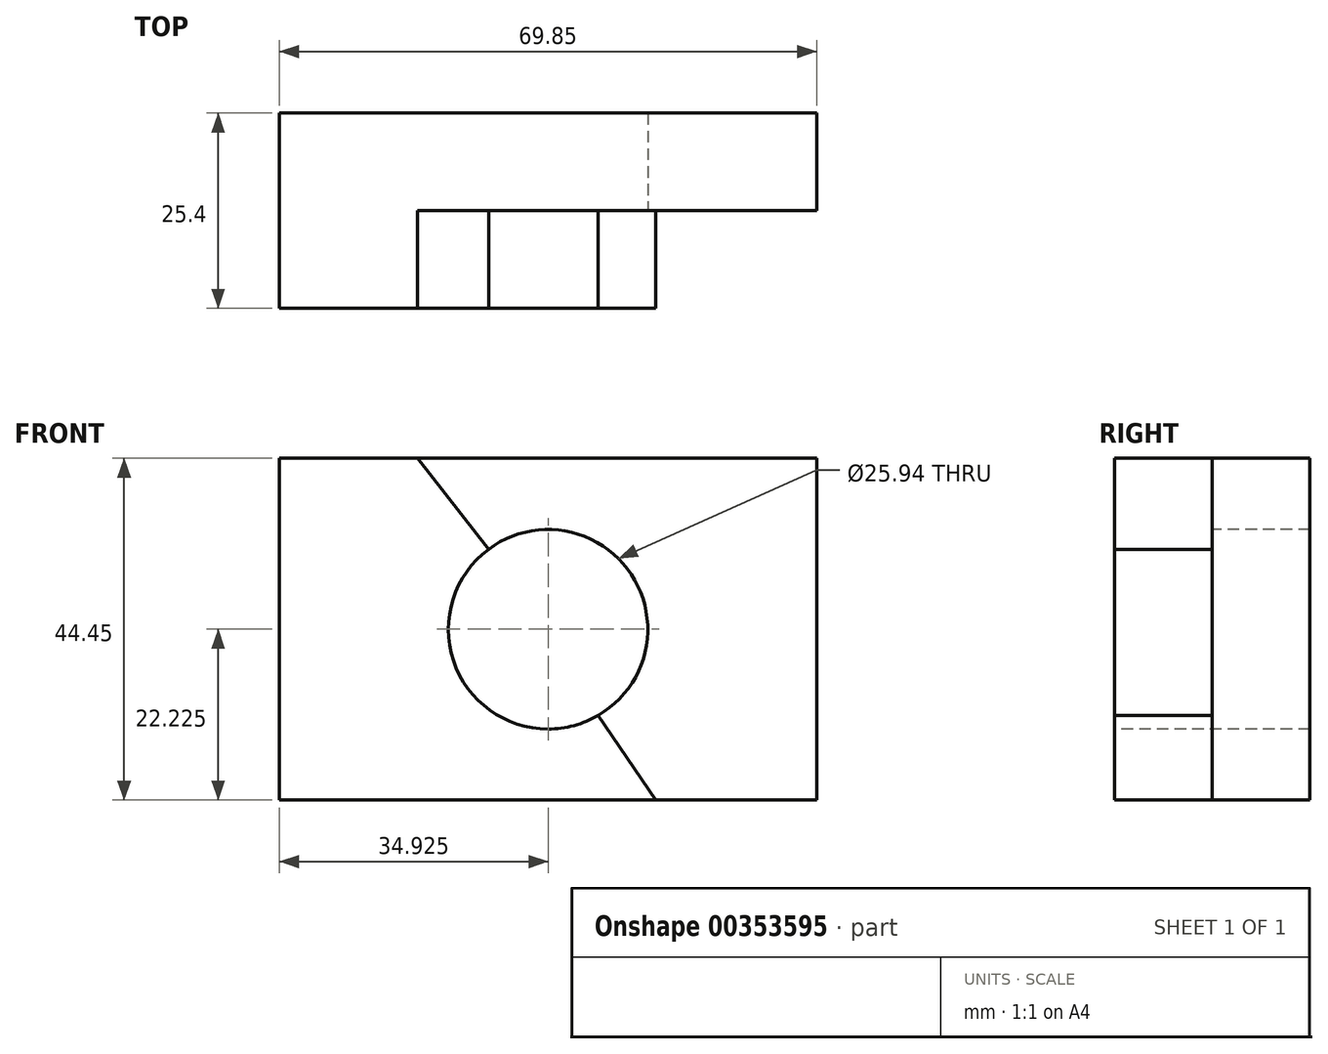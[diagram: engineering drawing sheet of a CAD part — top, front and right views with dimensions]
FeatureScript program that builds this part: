
annotation { "Feature Type Name" : "Feature", "Feature Type Description" : "" }
export const myFeature = defineFeature(function(context is Context, id is Id, definition is map)
    precondition{}
    {
        {
            var Q0;
            Q0=qCreatedBy(makeId("Front.planeOp"),FACE);
            var sketch = newSketch(context, id + "F0", { "sketchPlane" : qUnion([Q0])});
            skLineSegment(sketch, "E0.bottom", {"start": v(0, 0) * mm, "end": v(69.85, 0) * mm});
            skLineSegment(sketch, "E0.top", {"start": v(0, 44.45) * mm, "end": v(69.85, 44.45) * mm});
            skLineSegment(sketch, "E0.left", {"start": v(0, 0) * mm, "end": v(0, 44.45) * mm});
            skLineSegment(sketch, "E0.right", {"start": v(69.85, 0) * mm, "end": v(69.85, 44.45) * mm});
            skSolve(sketch);
        }
        {
            var Q0;
            Q0=makeQuery(id+"F0.imprint","IMPRINT",FACE,{"disambiguationData":[TD([[makeQuery(id+"F0.imprint","IMPRINT",EDGE,{"derivedFrom":sQuery(id+"F0.wireOp",EDGE,"E0.bottom")}),1.0]])]});
            extrude(context, id + "F1", {"entities" : qUnion([Q0]), "depth" : 12.7 * mm});
        }
        {
            var Q0;
            Q0=makeQuery(id+"F1.opExtrude","CAP_FACE",FACE,{"disambiguationData":[OSD([sQuery(id+"F0.wireOp",EDGE,"E0.bottom"),sQuery(id+"F0.wireOp",EDGE,"E0.top"),sQuery(id+"F0.wireOp",EDGE,"E0.left"),sQuery(id+"F0.wireOp",EDGE,"E0.right")])],"isStart":false});
            var sketch = newSketch(context, id + "F2", { "sketchPlane" : qUnion([Q0])});
            skCircle(sketch, "E1", {"center": v(34.92, 22.23) * mm, "radius": 12.97 * mm});
            skPoint(sketch, "E1.centerSnap0", {"position": v(69.85, 22.23) * mm});
            skPoint(sketch, "E1.centerSnap1", {"position": v(34.92, 44.45) * mm});
            skSolve(sketch);
        }
        {
            var Q0;
            Q0=makeQuery(id+"F2.imprint","IMPRINT",FACE,{"disambiguationData":[TD([[makeQuery(id+"F2.imprint","IMPRINT",EDGE,{"derivedFrom":sQuery(id+"F2.wireOp",EDGE,"E1")}),1.0]])]});
            extrude(context, id + "F3", {"entities" : qUnion([Q0]), "operationType" : NewBodyOperationType.REMOVE, "oppositeDirection" : true, "depth" : 25.4 * mm});
        }
        {
            var Q0;
            Q0=makeQuery(id+"F1.opExtrude","CAP_FACE",FACE,{"disambiguationData":[OSD([sQuery(id+"F0.wireOp",EDGE,"E0.bottom"),sQuery(id+"F0.wireOp",EDGE,"E0.top"),sQuery(id+"F0.wireOp",EDGE,"E0.left"),sQuery(id+"F0.wireOp",EDGE,"E0.right")])],"isStart":false});
            var sketch = newSketch(context, id + "F4", { "sketchPlane" : qUnion([Q0])});
            skLineSegment(sketch, "E2", {"start": v(17.95, 44.45) * mm, "end": v(0, 44.45) * mm});
            skLineSegment(sketch, "E3", {"start": v(0, 44.45) * mm, "end": v(0, 0) * mm});
            skLineSegment(sketch, "E4", {"start": v(0, 0) * mm, "end": v(48.9, 0) * mm});
            skLineSegment(sketch, "E5", {"start": v(48.9, 0) * mm, "end": v(41.45, 11.02) * mm});
            skLineSegment(sketch, "E6", {"start": v(17.95, 44.45) * mm, "end": v(27.18, 32.63) * mm});
            skSolve(sketch);
        }
        {
            var Q0;
            Q0=makeQuery(id+"F4.imprint","IMPRINT",FACE,{"disambiguationData":[TD([[makeQuery(id+"F4.imprint","IMPRINT",EDGE,{"derivedFrom":sQuery(id+"F4.wireOp",EDGE,"E2")}),-1.0]])]});
            extrude(context, id + "F5", {"entities" : qUnion([Q0]), "operationType" : NewBodyOperationType.ADD, "depth" : 12.7 * mm});
        }
    });
